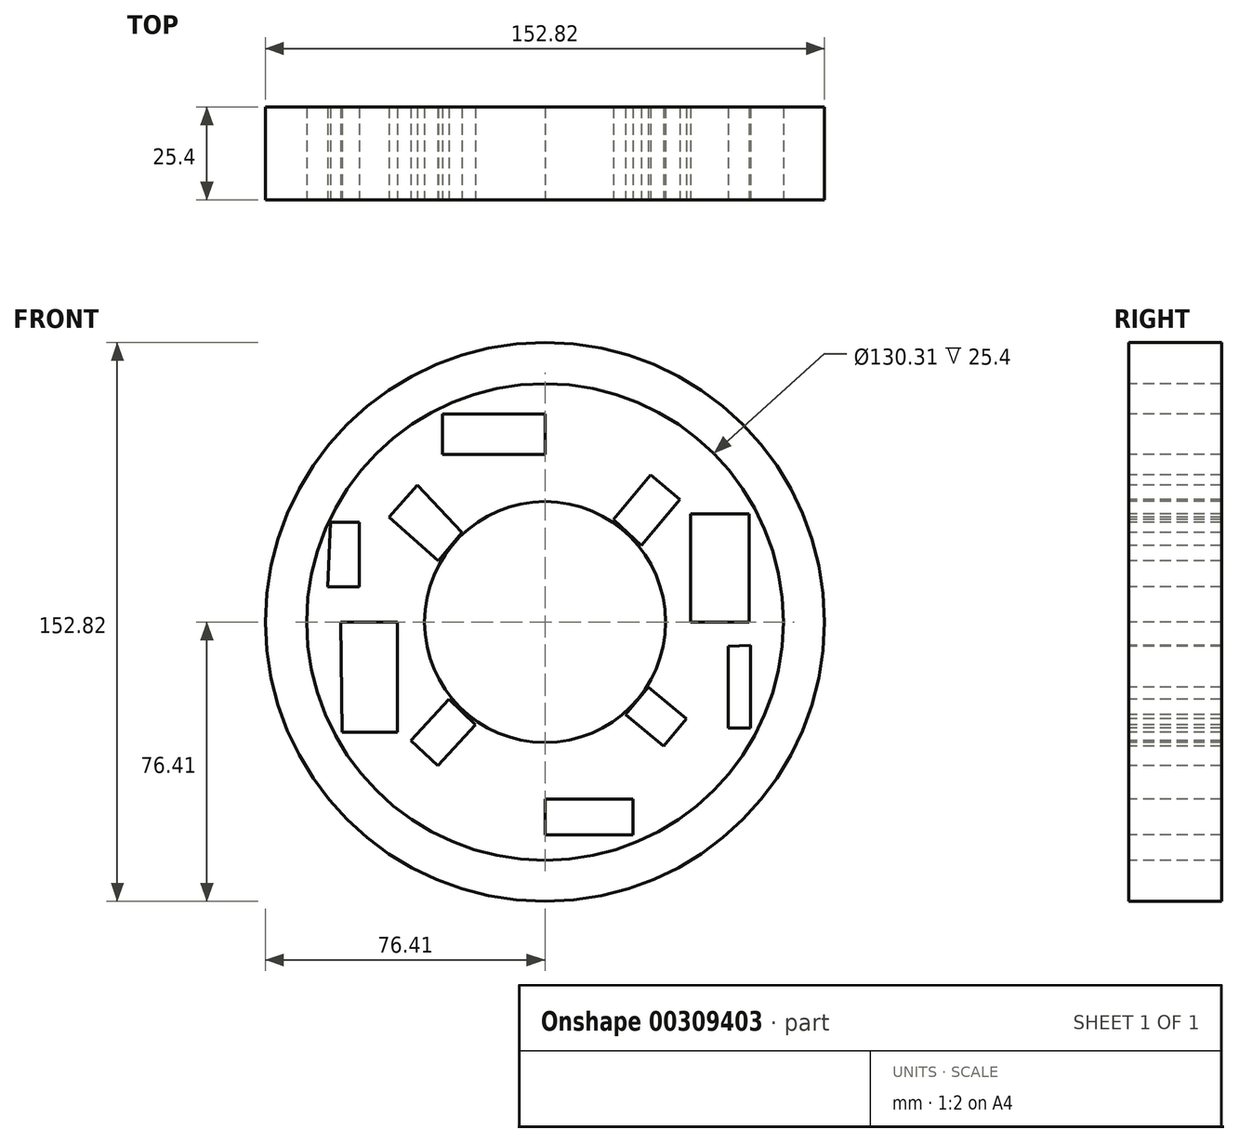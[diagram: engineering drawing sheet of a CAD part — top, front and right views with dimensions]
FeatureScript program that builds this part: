
annotation { "Feature Type Name" : "Feature", "Feature Type Description" : "" }
export const myFeature = defineFeature(function(context is Context, id is Id, definition is map)
    precondition{}
    {
        {
            var Q0;
            Q0=qCreatedBy(makeId("Front.planeOp"),FACE);
            var sketch = newSketch(context, id + "F0", { "sketchPlane" : qUnion([Q0])});
            skCircle(sketch, "E0", {"center": v(0, 0) * mm, "radius": 76.4 * mm});
            skCircle(sketch, "E1", {"center": v(0, 0) * mm, "radius": 65.15 * mm});
            skCircle(sketch, "E2", {"center": v(0, 0) * mm, "radius": 55.33 * mm});
            skCircle(sketch, "E3", {"center": v(0, 0) * mm, "radius": 45.71 * mm});
            skCircle(sketch, "E4", {"center": v(0, 0) * mm, "radius": 38.46 * mm});
            skCircle(sketch, "E5", {"center": v(0, 0) * mm, "radius": 30.87 * mm});
            skCircle(sketch, "E6", {"center": v(0, 0) * mm, "radius": 26.2 * mm});
            skCircle(sketch, "E7", {"center": v(0, 0) * mm, "radius": 20.98 * mm});
            skCircle(sketch, "E8", {"center": v(0, 0) * mm, "radius": 14.58 * mm});
            skCircle(sketch, "E9", {"center": v(0, 0) * mm, "radius": 9.35 * mm});
            skSolve(sketch);
        }
        {
            var Q0;
            Q0 = qSketchRegion(id + "F0", true);
            extrude(context, id + "F1", {"entities" : qUnion([Q0]), "oppositeDirection" : true, "depth" : 25.4 * mm});
        }
        {
            var Q0;
            Q0=qCreatedBy(makeId("Front.planeOp"),FACE);
            var sketch = newSketch(context, id + "F2", { "sketchPlane" : qUnion([Q0])});
            skCircle(sketch, "E10", {"center": v(0, 0) * mm, "radius": 32.93 * mm});
            skSolve(sketch);
        }
        {
            var Q0;
            Q0 = qSketchRegion(id + "F2", true);
            extrude(context, id + "F3", {"entities" : qUnion([Q0]), "oppositeDirection" : true, "depth" : 25.4 * mm});
        }
        {
            var Q0;
            Q0=qCreatedBy(makeId("Front.planeOp"),FACE);
            var sketch = newSketch(context, id + "F4", { "sketchPlane" : qUnion([Q0])});
            skLineSegment(sketch, "E11", {"start": v(-55.85, 0) * mm, "end": v(-40.34, 0) * mm});
            skLineSegment(sketch, "E12", {"start": v(-40.34, 0) * mm, "end": v(-40.34, -30.1) * mm});
            skLineSegment(sketch, "E13", {"start": v(-40.34, -30.1) * mm, "end": v(-55.4, -30.1) * mm});
            skLineSegment(sketch, "E14", {"start": v(-55.4, -30.1) * mm, "end": v(-55.85, 0) * mm});
            skLineSegment(sketch, "E15", {"start": v(39.78, 0) * mm, "end": v(39.78, 29.56) * mm});
            skLineSegment(sketch, "E16", {"start": v(39.78, 29.56) * mm, "end": v(55.78, 29.56) * mm});
            skLineSegment(sketch, "E17", {"start": v(55.78, 29.56) * mm, "end": v(55.78, 0) * mm});
            skLineSegment(sketch, "E18", {"start": v(55.78, 0) * mm, "end": v(39.78, 0) * mm});
            skSolve(sketch);
        }
        {
            var Q0;
            Q0 = qSketchRegion(id + "F4", true);
            extrude(context, id + "F5", {"entities" : qUnion([Q0]), "oppositeDirection" : true, "depth" : 25.4 * mm});
        }
        {
            var Q0;
            Q0 = qSketchRegion(id + "F4", true);
            extrude(context, id + "F6", {"entities" : qUnion([Q0]), "oppositeDirection" : true, "depth" : 25.4 * mm});
        }
        {
            var Q0;
            Q0=qCreatedBy(makeId("Front.planeOp"),FACE);
            var sketch = newSketch(context, id + "F7", { "sketchPlane" : qUnion([Q0])});
            skLineSegment(sketch, "E19", {"start": v(0, 56.9) * mm, "end": v(-28, 56.9) * mm});
            skLineSegment(sketch, "E20", {"start": v(-28, 56.9) * mm, "end": v(-28, 45.78) * mm});
            skLineSegment(sketch, "E21", {"start": v(-28, 45.78) * mm, "end": v(0, 45.78) * mm});
            skLineSegment(sketch, "E22", {"start": v(0, 45.78) * mm, "end": v(0, 56.9) * mm});
            skSolve(sketch);
        }
        {
            var Q0;
            Q0 = qSketchRegion(id + "F7", true);
            extrude(context, id + "F8", {"entities" : qUnion([Q0]), "oppositeDirection" : true, "depth" : 25.4 * mm});
        }
        {
            var Q0;
            Q0=qCreatedBy(makeId("Front.planeOp"),FACE);
            var sketch = newSketch(context, id + "F9", { "sketchPlane" : qUnion([Q0])});
            skLineSegment(sketch, "E23", {"start": v(0, -58.23) * mm, "end": v(24, -58.23) * mm});
            skLineSegment(sketch, "E24", {"start": v(24, -58.23) * mm, "end": v(24, -48.45) * mm});
            skLineSegment(sketch, "E25", {"start": v(24, -48.45) * mm, "end": v(0, -48.45) * mm});
            skLineSegment(sketch, "E26", {"start": v(0, -48.45) * mm, "end": v(0, -58.23) * mm});
            skSolve(sketch);
        }
        {
            var Q0;
            Q0 = qSketchRegion(id + "F9", true);
            extrude(context, id + "F10", {"entities" : qUnion([Q0]), "oppositeDirection" : true, "depth" : 25.4 * mm});
        }
        {
            var Q0;
            Q0=qCreatedBy(makeId("Front.planeOp"),FACE);
            var sketch = newSketch(context, id + "F11", { "sketchPlane" : qUnion([Q0])});
            skLineSegment(sketch, "E27", {"start": v(-29.11, 16.67) * mm, "end": v(-42.67, 28.67) * mm});
            skLineSegment(sketch, "E28", {"start": v(-42.67, 28.67) * mm, "end": v(-34.88, 37.47) * mm});
            skLineSegment(sketch, "E29", {"start": v(-34.88, 37.47) * mm, "end": v(-22.67, 24.45) * mm});
            skLineSegment(sketch, "E30", {"start": v(-22.67, 24.45) * mm, "end": v(-29.11, 16.67) * mm});
            skSolve(sketch);
        }
        {
            var Q0;
            Q0 = qSketchRegion(id + "F11", true);
            extrude(context, id + "F12", {"entities" : qUnion([Q0]), "oppositeDirection" : true, "depth" : 25.4 * mm});
        }
        {
            var Q0;
            Q0=qCreatedBy(makeId("Front.planeOp"),FACE);
            var sketch = newSketch(context, id + "F13", { "sketchPlane" : qUnion([Q0])});
            skLineSegment(sketch, "E31", {"start": v(18.67, 28) * mm, "end": v(28.9, 40.23) * mm});
            skLineSegment(sketch, "E32", {"start": v(28.9, 40.23) * mm, "end": v(36.88, 33.54) * mm});
            skLineSegment(sketch, "E33", {"start": v(36.88, 33.54) * mm, "end": v(26.32, 20.92) * mm});
            skLineSegment(sketch, "E34", {"start": v(26.32, 20.92) * mm, "end": v(18.67, 28) * mm});
            skSolve(sketch);
        }
        {
            var Q0;
            Q0 = qSketchRegion(id + "F13", true);
            extrude(context, id + "F14", {"entities" : qUnion([Q0]), "oppositeDirection" : true, "depth" : 25.4 * mm});
        }
        {
            var Q0;
            Q0=qCreatedBy(makeId("Front.planeOp"),FACE);
            var sketch = newSketch(context, id + "F15", { "sketchPlane" : qUnion([Q0])});
            skLineSegment(sketch, "E35", {"start": v(22, -25.34) * mm, "end": v(32.45, -34) * mm});
            skLineSegment(sketch, "E36", {"start": v(32.45, -34) * mm, "end": v(38.68, -26.5) * mm});
            skLineSegment(sketch, "E37", {"start": v(38.68, -26.5) * mm, "end": v(28.18, -17.78) * mm});
            skLineSegment(sketch, "E38", {"start": v(28.18, -17.78) * mm, "end": v(22, -25.34) * mm});
            skSolve(sketch);
        }
        {
            var Q0;
            Q0 = qSketchRegion(id + "F15", true);
            extrude(context, id + "F16", {"entities" : qUnion([Q0]), "oppositeDirection" : true, "depth" : 25.4 * mm});
        }
        {
            var Q0;
            Q0=qCreatedBy(makeId("Front.planeOp"),FACE);
            var sketch = newSketch(context, id + "F17", { "sketchPlane" : qUnion([Q0])});
            skLineSegment(sketch, "E39", {"start": v(-26.22, -21.11) * mm, "end": v(-36.67, -32.45) * mm});
            skLineSegment(sketch, "E40", {"start": v(-36.67, -32.45) * mm, "end": v(-29.26, -39.27) * mm});
            skLineSegment(sketch, "E41", {"start": v(-29.26, -39.27) * mm, "end": v(-19.02, -28.16) * mm});
            skLineSegment(sketch, "E42", {"start": v(-19.02, -28.16) * mm, "end": v(-26.22, -21.11) * mm});
            skSolve(sketch);
        }
        {
            var Q0;
            Q0 = qSketchRegion(id + "F17", true);
            extrude(context, id + "F18", {"entities" : qUnion([Q0]), "oppositeDirection" : true, "depth" : 25.4 * mm});
        }
        {
            var Q0;
            Q0=qCreatedBy(makeId("Front.planeOp"),FACE);
            var sketch = newSketch(context, id + "F19", { "sketchPlane" : qUnion([Q0])});
            skLineSegment(sketch, "E43", {"start": v(-59.43, 9.66) * mm, "end": v(-50.76, 9.66) * mm});
            skLineSegment(sketch, "E44", {"start": v(-50.76, 9.66) * mm, "end": v(-50.76, 27.24) * mm});
            skLineSegment(sketch, "E45", {"start": v(-50.76, 27.24) * mm, "end": v(-58.69, 27.24) * mm});
            skLineSegment(sketch, "E46", {"start": v(-58.69, 27.24) * mm, "end": v(-59.43, 9.66) * mm});
            skSolve(sketch);
        }
        {
            var Q0;
            Q0 = qSketchRegion(id + "F19", true);
            extrude(context, id + "F20", {"entities" : qUnion([Q0]), "oppositeDirection" : true, "depth" : 25.4 * mm});
        }
        {
            var Q0;
            Q0=qCreatedBy(makeId("Front.planeOp"),FACE);
            var sketch = newSketch(context, id + "F21", { "sketchPlane" : qUnion([Q0])});
            skLineSegment(sketch, "E47", {"start": v(50.02, -6.69) * mm, "end": v(50.02, -28.97) * mm});
            skLineSegment(sketch, "E48", {"start": v(50.02, -28.97) * mm, "end": v(56.2, -28.97) * mm});
            skLineSegment(sketch, "E49", {"start": v(56.2, -28.97) * mm, "end": v(56.2, -6.44) * mm});
            skLineSegment(sketch, "E50", {"start": v(56.2, -6.44) * mm, "end": v(50.02, -6.69) * mm});
            skSolve(sketch);
        }
        {
            var Q0;
            Q0 = qSketchRegion(id + "F21", true);
            extrude(context, id + "F22", {"entities" : qUnion([Q0]), "oppositeDirection" : true, "depth" : 25.4 * mm});
        }
    });
